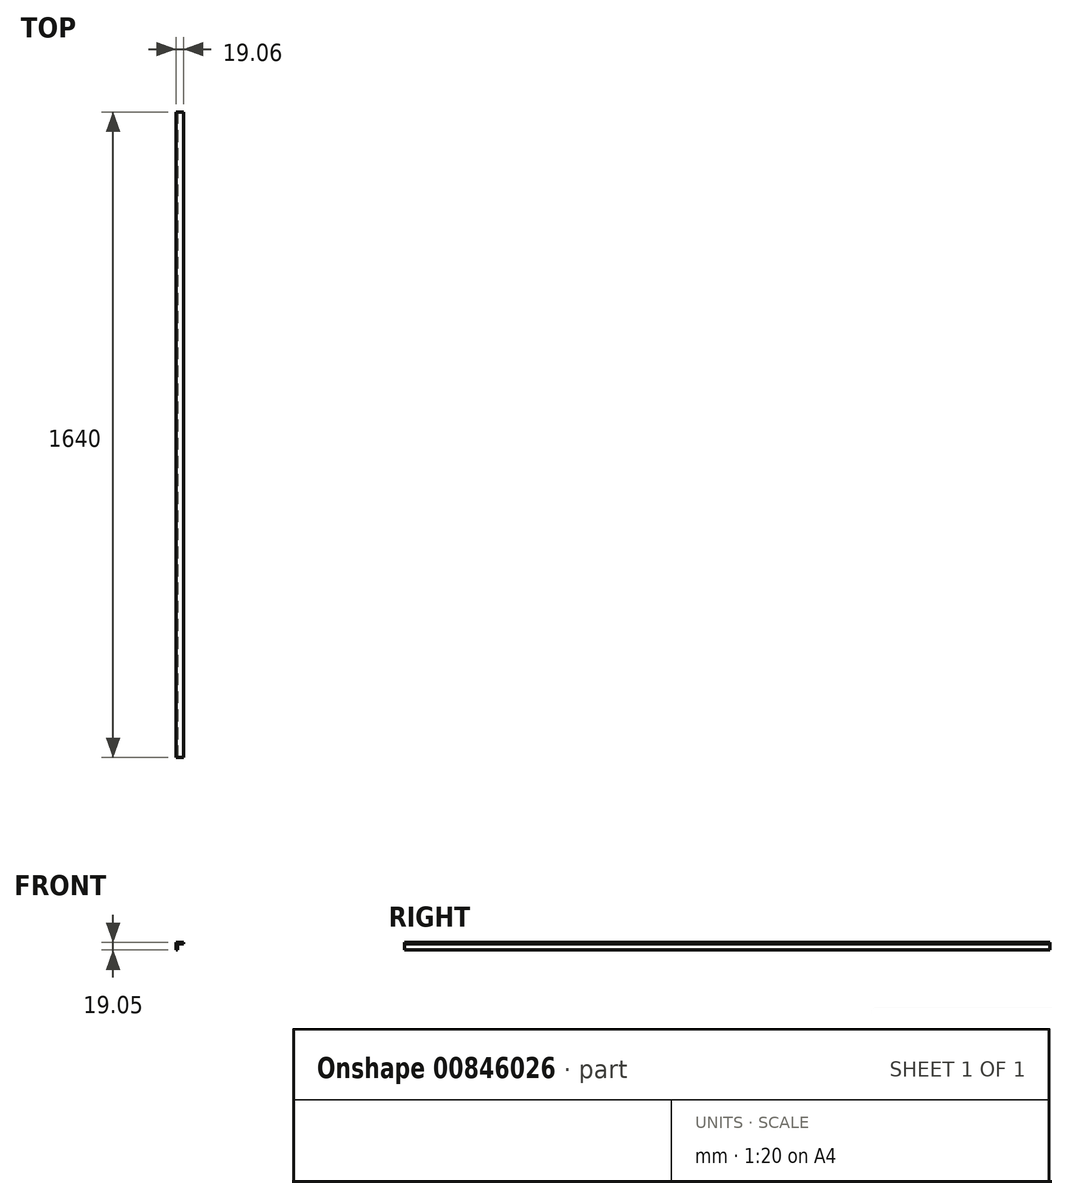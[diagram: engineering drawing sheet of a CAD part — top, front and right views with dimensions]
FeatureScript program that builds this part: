
annotation { "Feature Type Name" : "Feature", "Feature Type Description" : "" }
export const myFeature = defineFeature(function(context is Context, id is Id, definition is map)
    precondition{}
    {
        {
            var Q0;
            Q0=qCreatedBy(makeId("Front.planeOp"),FACE);
            var sketch = newSketch(context, id + "F0", { "sketchPlane" : qUnion([Q0])});
            skLineSegment(sketch, "E0", {"start": v(-9.52, 0) * mm, "end": v(-9.52, -19.05) * mm});
            skLineSegment(sketch, "E1", {"start": v(-9.52, -19.05) * mm, "end": v(-6.35, -19.05) * mm});
            skLineSegment(sketch, "E2", {"start": v(-6.35, -19.05) * mm, "end": v(-6.35, -3.18) * mm});
            skLineSegment(sketch, "E3", {"start": v(-6.35, -3.18) * mm, "end": v(9.53, -3.17) * mm});
            skLineSegment(sketch, "E4", {"start": v(9.53, -3.17) * mm, "end": v(9.52, 0) * mm});
            skLineSegment(sketch, "E5", {"start": v(9.52, 0) * mm, "end": v(-9.52, 0) * mm});
            skSolve(sketch);
        }
        {
            var Q0;
            Q0 = qSketchRegion(id + "F0", true);
            extrude(context, id + "F1", {"entities" : qUnion([Q0]), "oppositeDirection" : true, "depth" : 1640 * mm, "offsetDistance" : 25.4 * mm});
        }
    });
